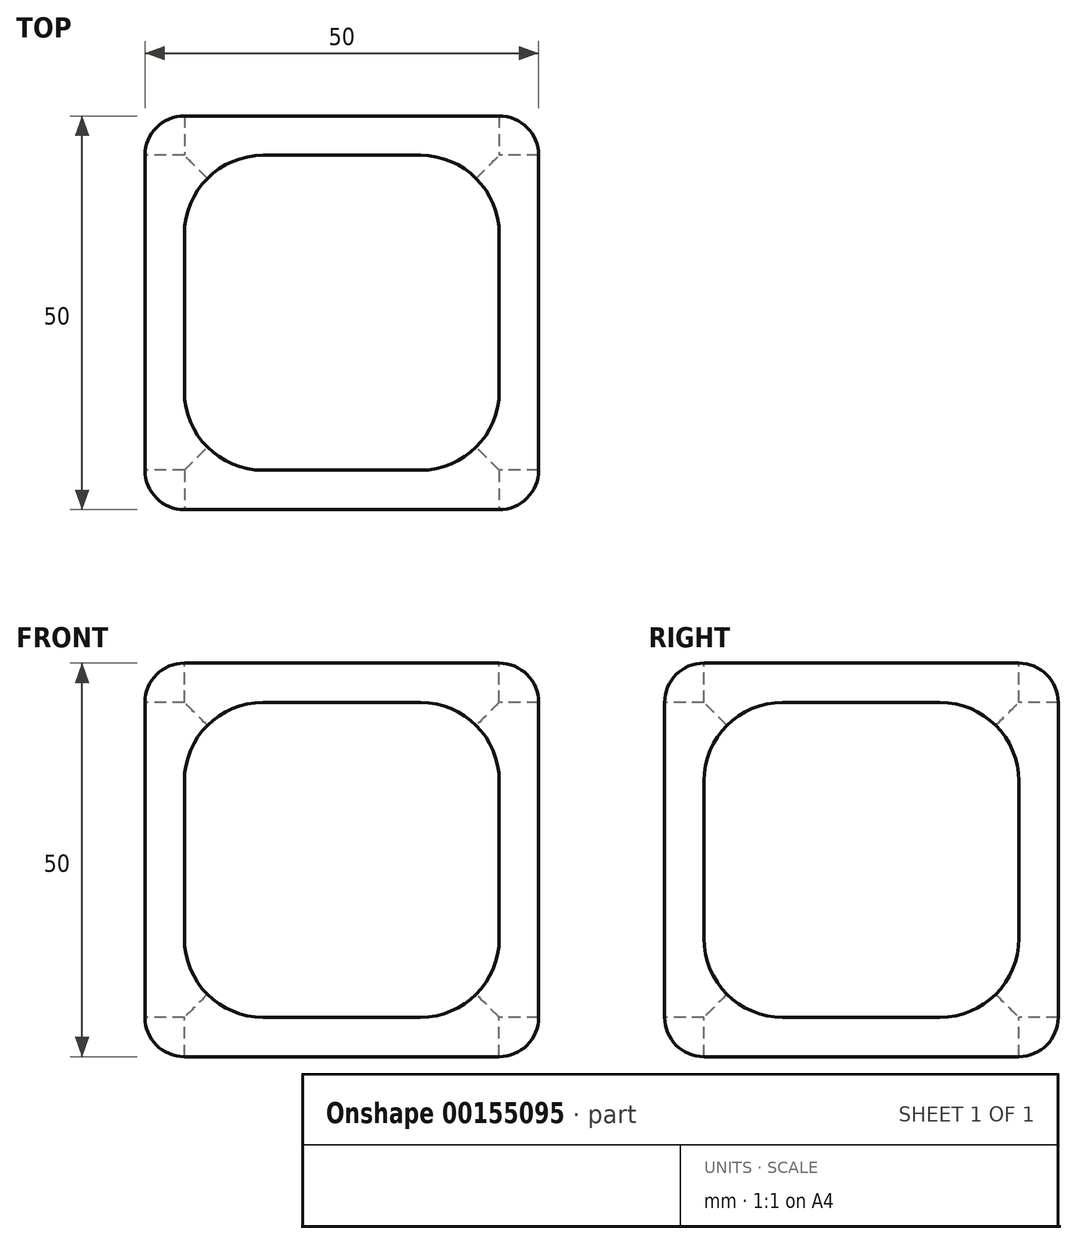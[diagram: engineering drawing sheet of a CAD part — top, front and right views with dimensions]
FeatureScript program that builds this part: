
annotation { "Feature Type Name" : "Feature", "Feature Type Description" : "" }
export const myFeature = defineFeature(function(context is Context, id is Id, definition is map)
    precondition{}
    {
        {
            var Q0;
            Q0=qCreatedBy(makeId("Top.planeOp"),FACE);
            var sketch = newSketch(context, id + "F0", { "sketchPlane" : qUnion([Q0])});
            skLineSegment(sketch, "E0.bottom", {"start": v(25, 25) * mm, "end": v(-25, 25) * mm});
            skLineSegment(sketch, "E0.top", {"start": v(25, -25) * mm, "end": v(-25, -25) * mm});
            skLineSegment(sketch, "E0.left", {"start": v(25, 25) * mm, "end": v(25, -25) * mm});
            skLineSegment(sketch, "E0.right", {"start": v(-25, 25) * mm, "end": v(-25, -25) * mm});
            skPoint(sketch, "E0.middle", {"position": v(0, 0) * mm});
            skSolve(sketch);
        }
        {
            var Q0;
            Q0 = qSketchRegion(id + "F0", true);
            extrude(context, id + "F1", {"entities" : qUnion([Q0]), "depth" : 50 * mm});
        }
        {
            var Q0;
            Q0=makeQuery(id+"F1.opExtrude","CAP_FACE",FACE,{"disambiguationData":[OSD([sQuery(id+"F0.wireOp",EDGE,"E0.bottom"),sQuery(id+"F0.wireOp",EDGE,"E0.top"),sQuery(id+"F0.wireOp",EDGE,"E0.left"),sQuery(id+"F0.wireOp",EDGE,"E0.right")])],"isStart":false});
            var sketch = newSketch(context, id + "F2", { "sketchPlane" : qUnion([Q0])});
            skLineSegment(sketch, "E1.bottom", {"start": v(10, 20) * mm, "end": v(-10, 20) * mm});
            skLineSegment(sketch, "E1.top", {"start": v(10, -20) * mm, "end": v(-10, -20) * mm});
            skLineSegment(sketch, "E1.left", {"start": v(20, 10) * mm, "end": v(20, -10) * mm});
            skLineSegment(sketch, "E1.right", {"start": v(-20, 10) * mm, "end": v(-20, -10) * mm});
            skPoint(sketch, "E1.middle", {"position": v(0, 0) * mm});
            skPoint(sketch, "E2.visualSharp", {"position": v(-20, 20) * mm});
            skArc(sketch, "E2.filletArc", {"start": v(-10, 20) * mm, "mid": v(-17.07, 17.07) * mm, "end": v(-20, 10) * mm});
            skPoint(sketch, "E3.visualSharp", {"position": v(20, -20) * mm});
            skArc(sketch, "E3.filletArc", {"start": v(10, -20) * mm, "mid": v(17.07, -17.07) * mm, "end": v(20, -10) * mm});
            skPoint(sketch, "E4.visualSharp", {"position": v(20, 20) * mm});
            skArc(sketch, "E4.filletArc", {"start": v(20, 10) * mm, "mid": v(17.07, 17.07) * mm, "end": v(10, 20) * mm});
            skPoint(sketch, "E5.visualSharp", {"position": v(-20, -20) * mm});
            skArc(sketch, "E5.filletArc", {"start": v(-20, -10) * mm, "mid": v(-17.07, -17.07) * mm, "end": v(-10, -20) * mm});
            skSolve(sketch);
        }
        {
            var Q0;
            Q0 = qSketchRegion(id + "F2", true);
            extrude(context, id + "F3", {"entities" : qUnion([Q0]), "operationType" : NewBodyOperationType.REMOVE, "endBound" : BoundingType.THROUGH_ALL, "oppositeDirection" : true, "depth" : 25.4 * mm});
        }
        {
            var Q0;
            Q0=makeQuery(id+"F1.opExtrude","SWEPT_FACE",FACE,{"disambiguationData":[OSD([sQuery(id+"F0.wireOp",EDGE,"E0.right")])]});
            var sketch = newSketch(context, id + "F4", { "sketchPlane" : qUnion([Q0])});
            skLineSegment(sketch, "E6.bottom", {"start": v(-10, 45) * mm, "end": v(10, 45) * mm});
            skLineSegment(sketch, "E6.top", {"start": v(-10, 5) * mm, "end": v(10, 5) * mm});
            skLineSegment(sketch, "E6.left", {"start": v(-20, 35) * mm, "end": v(-20, 15) * mm});
            skLineSegment(sketch, "E6.right", {"start": v(20, 35) * mm, "end": v(20, 15) * mm});
            skPoint(sketch, "E7.visualSharp", {"position": v(-20, 45) * mm});
            skArc(sketch, "E7.filletArc", {"start": v(-10, 45) * mm, "mid": v(-17.07, 42.07) * mm, "end": v(-20, 35) * mm});
            skPoint(sketch, "E8.visualSharp", {"position": v(20, 45) * mm});
            skArc(sketch, "E8.filletArc", {"start": v(20, 35) * mm, "mid": v(17.07, 42.07) * mm, "end": v(10, 45) * mm});
            skPoint(sketch, "E9.visualSharp", {"position": v(20, 5) * mm});
            skArc(sketch, "E9.filletArc", {"start": v(10, 5) * mm, "mid": v(17.07, 7.93) * mm, "end": v(20, 15) * mm});
            skPoint(sketch, "E10.visualSharp", {"position": v(-20, 5) * mm});
            skArc(sketch, "E10.filletArc", {"start": v(-20, 15) * mm, "mid": v(-17.07, 7.93) * mm, "end": v(-10, 5) * mm});
            skSolve(sketch);
        }
        {
            var Q0;
            Q0 = qSketchRegion(id + "F4", true);
            extrude(context, id + "F5", {"entities" : qUnion([Q0]), "operationType" : NewBodyOperationType.REMOVE, "endBound" : BoundingType.THROUGH_ALL, "oppositeDirection" : true, "depth" : 25.4 * mm});
        }
        {
            var Q0;
            Q0=makeQuery(id+"F1.opExtrude","SWEPT_FACE",FACE,{"disambiguationData":[OSD([sQuery(id+"F0.wireOp",EDGE,"E0.top")])]});
            var sketch = newSketch(context, id + "F6", { "sketchPlane" : qUnion([Q0])});
            skLineSegment(sketch, "E11.bottom", {"start": v(-10, 45) * mm, "end": v(10, 45) * mm});
            skLineSegment(sketch, "E11.top", {"start": v(-10, 5) * mm, "end": v(10, 5) * mm});
            skLineSegment(sketch, "E11.left", {"start": v(-20, 35) * mm, "end": v(-20, 15) * mm});
            skLineSegment(sketch, "E11.right", {"start": v(20, 35) * mm, "end": v(20, 15) * mm});
            skPoint(sketch, "E12.visualSharp", {"position": v(-20, 45) * mm});
            skArc(sketch, "E12.filletArc", {"start": v(-10, 45) * mm, "mid": v(-17.07, 42.07) * mm, "end": v(-20, 35) * mm});
            skPoint(sketch, "E13.visualSharp", {"position": v(20, 45) * mm});
            skArc(sketch, "E13.filletArc", {"start": v(20, 35) * mm, "mid": v(17.07, 42.07) * mm, "end": v(10, 45) * mm});
            skPoint(sketch, "E14.visualSharp", {"position": v(-20, 5) * mm});
            skArc(sketch, "E14.filletArc", {"start": v(-20, 15) * mm, "mid": v(-17.07, 7.93) * mm, "end": v(-10, 5) * mm});
            skPoint(sketch, "E15.visualSharp", {"position": v(20, 5) * mm});
            skArc(sketch, "E15.filletArc", {"start": v(10, 5) * mm, "mid": v(17.07, 7.93) * mm, "end": v(20, 15) * mm});
            skSolve(sketch);
        }
        {
            var Q0;
            Q0 = qSketchRegion(id + "F6", true);
            extrude(context, id + "F7", {"entities" : qUnion([Q0]), "operationType" : NewBodyOperationType.REMOVE, "endBound" : BoundingType.THROUGH_ALL, "oppositeDirection" : true, "depth" : 25.4 * mm});
        }
        {
            var Q0;
            Q0=makeQuery(id+"F1.opExtrude","CAP_EDGE",EDGE,{"disambiguationData":[OSD([sQuery(id+"F0.wireOp",EDGE,"E0.bottom")])],"isStart":true});
            var Q1;
            Q1=makeQuery(id+"F1.opExtrude","CAP_EDGE",EDGE,{"disambiguationData":[OSD([sQuery(id+"F0.wireOp",EDGE,"E0.right")])],"isStart":true});
            var Q2;
            Q2=makeQuery(id+"F1.opExtrude","CAP_EDGE",EDGE,{"disambiguationData":[OSD([sQuery(id+"F0.wireOp",EDGE,"E0.top")])],"isStart":true});
            var Q3;
            Q3=makeQuery(id+"F1.opExtrude","CAP_EDGE",EDGE,{"disambiguationData":[OSD([sQuery(id+"F0.wireOp",EDGE,"E0.left")])],"isStart":true});
            var Q4;
            Q4=makeQuery(id+"F1.opExtrude","SWEPT_EDGE",EDGE,{"disambiguationData":[OSD([sQuery(id+"F0.wireOp",EDGE,"E0.bottom"),sQuery(id+"F0.wireOp",EDGE,"E0.left")])]});
            var Q5;
            Q5=makeQuery(id+"F1.opExtrude","SWEPT_EDGE",EDGE,{"disambiguationData":[OSD([sQuery(id+"F0.wireOp",EDGE,"E0.bottom"),sQuery(id+"F0.wireOp",EDGE,"E0.right")])]});
            var Q6;
            Q6=makeQuery(id+"F1.opExtrude","SWEPT_EDGE",EDGE,{"disambiguationData":[OSD([sQuery(id+"F0.wireOp",EDGE,"E0.top"),sQuery(id+"F0.wireOp",EDGE,"E0.right")])]});
            var Q7;
            Q7=makeQuery(id+"F1.opExtrude","CAP_EDGE",EDGE,{"disambiguationData":[OSD([sQuery(id+"F0.wireOp",EDGE,"E0.bottom")])],"isStart":false});
            var Q8;
            Q8=makeQuery(id+"F1.opExtrude","CAP_EDGE",EDGE,{"disambiguationData":[OSD([sQuery(id+"F0.wireOp",EDGE,"E0.right")])],"isStart":false});
            var Q9;
            Q9=makeQuery(id+"F1.opExtrude","CAP_EDGE",EDGE,{"disambiguationData":[OSD([sQuery(id+"F0.wireOp",EDGE,"E0.top")])],"isStart":false});
            var Q10;
            Q10=makeQuery(id+"F1.opExtrude","CAP_EDGE",EDGE,{"disambiguationData":[OSD([sQuery(id+"F0.wireOp",EDGE,"E0.left")])],"isStart":false});
            var Q11;
            Q11=makeQuery(id+"F1.opExtrude","SWEPT_EDGE",EDGE,{"disambiguationData":[OSD([sQuery(id+"F0.wireOp",EDGE,"E0.top"),sQuery(id+"F0.wireOp",EDGE,"E0.left")])]});
            fillet(context, id + "F8", {"entities" : qUnion([Q0, Q1, Q2, Q3, Q4, Q5, Q6, Q7, Q8, Q9, Q10, Q11]), "radius" : 5 * mm, "tangentPropagation" : true, "allowEdgeOverflow" : false});
        }
    });
